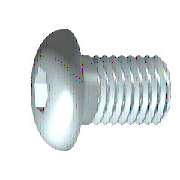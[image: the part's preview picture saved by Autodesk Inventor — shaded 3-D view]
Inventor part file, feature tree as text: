
AUTODESK INVENTOR PART (.ipt)
format: ipt  version: 2025 (Build 290162010, 162A)  size: 198,144 bytes
history: native  units: mm (DEFAULTED — no unit token found)
features: extrude x1, plane x1, fillet x1
ambient origin geometry x7: Origin, YZ Plane, XY Plane, X Axis, Y Axis, Z Axis, Center Point
bodies: Solid1 (feature_tree), Body (feature_tree)
feature tree (3):
  extrude  "Slot"  Depth=6.5mm
  plane  "Work Plane1"
  fillet  "Fillet2"  Radius=0.306825mm
